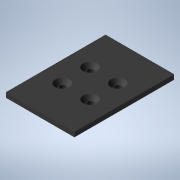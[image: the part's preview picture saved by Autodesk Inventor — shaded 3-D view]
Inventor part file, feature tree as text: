
AUTODESK INVENTOR PART (.ipt)
format: ipt  version: 2020 (Build 240168000, 168)  size: 134,656 bytes
history: native  units: in
note: dims shown in document units (in); Inventor stores cm internally (conversion verified against a paired STEP export)
features: sketch x3, extrude x2, hole x1, fillet x1
ambient origin geometry x8: Origin, YZ Plane, XZ Plane, XY Plane, X Axis, Y Axis, Z Axis, Center Point
bodies: Solid1 (feature_tree)
feature tree (7):
  extrude  "Extrusion1"  Depth=3.58in
  extrude  "Extrusion2"  Depth=0.17in
  hole  "Hole1"  [1 undecoded]
  fillet  "Fillet1"  Radius=1.75in
  sketch  "Sketch1"  dims[d0=2.46in d1=3.58in]
  sketch  "Sketch2"  dims[d2=0.17in d3=0.0in d4=1.0in]
  sketch  "Sketch3"  dims[d5=1.0in d6=0.266in d7=0.75in d8=0.507in d9=0.188in d10=0.5635in d11=1.0in d12=0.8108in d13=1.75in d14=1.75in d15=0.25in d16=0.0in d17=0.125in]
note: 1 required parameter value undecoded (feature->parameter linkage not recoverable at this tier; creation-order binding heuristic only, values carry confidence <= 0.55)
